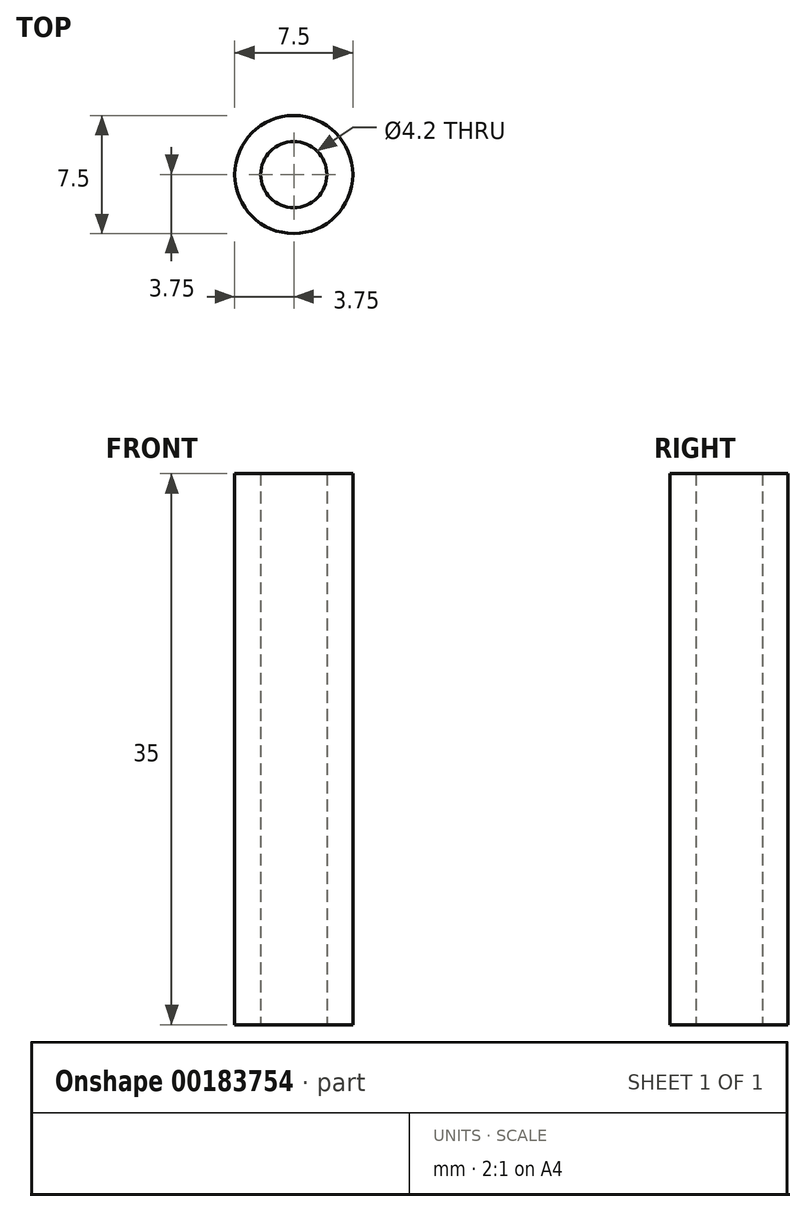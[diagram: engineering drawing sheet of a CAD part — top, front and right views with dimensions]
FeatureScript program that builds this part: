
annotation { "Feature Type Name" : "Feature", "Feature Type Description" : "" }
export const myFeature = defineFeature(function(context is Context, id is Id, definition is map)
    precondition{}
    {
        {
            var Q0;
            Q0=qCreatedBy(makeId("Top.planeOp"),FACE);
            var sketch = newSketch(context, id + "F0", { "sketchPlane" : qUnion([Q0])});
            skCircle(sketch, "E0", {"center": v(0, 0) * mm, "radius": 3.75 * mm});
            skCircle(sketch, "E1", {"center": v(0, 0) * mm, "radius": 2.1 * mm});
            skSolve(sketch);
        }
        {
            var Q0;
            Q0 = qSketchRegion(id + "F0", true);
            extrude(context, id + "F1", {"entities" : qUnion([Q0]), "depth" : 35 * mm});
        }
    });
